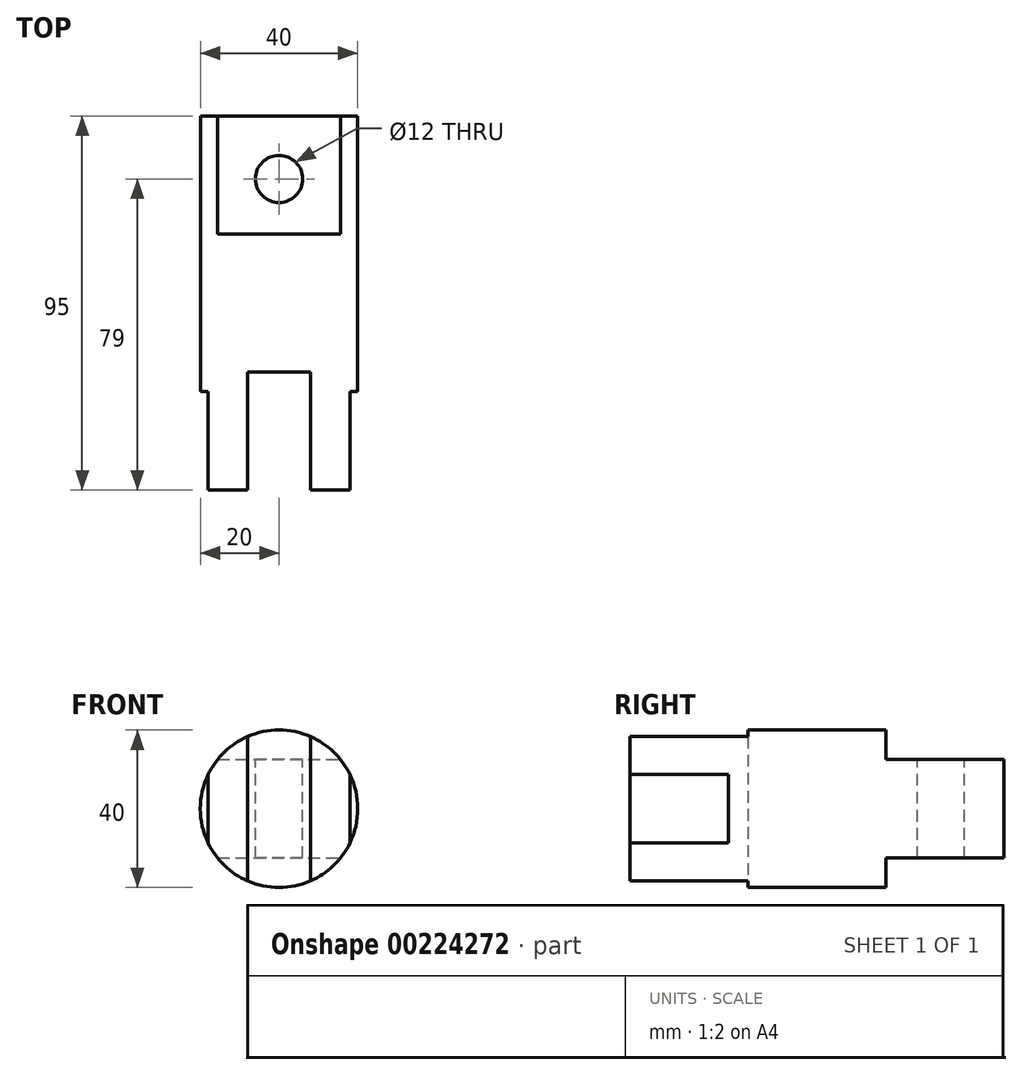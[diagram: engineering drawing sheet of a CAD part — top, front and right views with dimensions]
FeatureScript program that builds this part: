
annotation { "Feature Type Name" : "Feature", "Feature Type Description" : "" }
export const myFeature = defineFeature(function(context is Context, id is Id, definition is map)
    precondition{}
    {
        {
            var Q0;
            Q0=qCreatedBy(makeId("Front.planeOp"),FACE);
            var sketch = newSketch(context, id + "F0", { "sketchPlane" : qUnion([Q0])});
            skCircle(sketch, "E0", {"center": v(0, 0) * mm, "radius": 20 * mm});
            skSolve(sketch);
        }
        {
            var Q0;
            Q0=makeQuery(id+"F0.imprint","IMPRINT",FACE,{"disambiguationData":[TD([[makeQuery(id+"F0.imprint","IMPRINT",EDGE,{"derivedFrom":sQuery(id+"F0.wireOp",EDGE,"E0")}),1.0]])]});
            extrude(context, id + "F1", {"entities" : qUnion([Q0]), "endBound" : BoundingType.SYMMETRIC, "depth" : 95 * mm});
        }
        {
            var Q0;
            Q0=makeQuery(id+"F1.opExtrude","CAP_FACE",FACE,{"disambiguationData":[OSD([sQuery(id+"F0.wireOp",EDGE,"E0")])],"isStart":false});
            var sketch = newSketch(context, id + "F2", { "sketchPlane" : qUnion([Q0])});
            skLineSegment(sketch, "E1", {"start": v(-8, 18.33) * mm, "end": v(-8, -18.33) * mm});
            skLineSegment(sketch, "E2.MirrorCS", {"start": v(8, 18.33) * mm, "end": v(8, -18.33) * mm});
            skCircle(sketch, "E3.0", {"center": v(0, 0) * mm, "radius": 20 * mm});
            skSolve(sketch);
        }
        {
            var Q0;
            {var subQ0=sQuery(id+"F2.wireOp",EDGE,"E1");Q0=makeQuery(id+"F2.imprint","IMPRINT",FACE,{"disambiguationData":[TD([[makeQuery(id+"F2.imprint","IMPRINT",EDGE,{"derivedFrom":subQ0}),1.0]])]});}
            extrude(context, id + "F3", {"entities" : qUnion([Q0]), "operationType" : NewBodyOperationType.REMOVE, "oppositeDirection" : true, "depth" : 30 * mm});
        }
        {
            var Q0;
            {var subQ0=sQuery(id+"F2.wireOp",EDGE,"E2.MirrorCS");Q0=makeQuery(id+"F2.imprint","IMPRINT",FACE,{"disambiguationData":[TD([[makeQuery(id+"F2.imprint","IMPRINT",EDGE,{"derivedFrom":subQ0}),1.0]])]});}
            var sketch = newSketch(context, id + "F4", { "sketchPlane" : qUnion([Q0])});
            skLineSegment(sketch, "E4", {"start": v(18, 8.72) * mm, "end": v(18, -8.72) * mm});
            skCircle(sketch, "E5.0", {"center": v(0, 0) * mm, "radius": 20 * mm});
            skLineSegment(sketch, "E6.MirrorCS", {"start": v(-18, 8.72) * mm, "end": v(-18, -8.72) * mm});
            skSolve(sketch);
        }
        {
            var Q0;
            {var subQ0=sQuery(id+"F4.wireOp",EDGE,"E6.MirrorCS");Q0=makeQuery(id+"F4.imprint","IMPRINT",FACE,{"disambiguationData":[TD([[makeQuery(id+"F4.imprint","IMPRINT",EDGE,{"derivedFrom":subQ0}),-1.0]])]});}
            var Q1;
            {var subQ0=sQuery(id+"F4.wireOp",EDGE,"E4");Q1=makeQuery(id+"F4.imprint","IMPRINT",FACE,{"disambiguationData":[TD([[makeQuery(id+"F4.imprint","IMPRINT",EDGE,{"derivedFrom":subQ0}),1.0]])]});}
            extrude(context, id + "F5", {"entities" : qUnion([Q0, Q1]), "operationType" : NewBodyOperationType.REMOVE, "oppositeDirection" : true, "depth" : 25 * mm});
        }
        {
            var Q0;
            Q0=makeQuery(id+"F1.opExtrude","CAP_FACE",FACE,{"disambiguationData":[OSD([sQuery(id+"F0.wireOp",EDGE,"E0")])],"isStart":true});
            var sketch = newSketch(context, id + "F6", { "sketchPlane" : qUnion([Q0])});
            skLineSegment(sketch, "E7", {"start": v(15.61, 12.5) * mm, "end": v(-15.61, 12.5) * mm});
            skLineSegment(sketch, "E8", {"start": v(15.61, -12.5) * mm, "end": v(-15.61, -12.5) * mm});
            skCircle(sketch, "E9.0", {"center": v(0, 0) * mm, "radius": 20 * mm});
            skSolve(sketch);
        }
        {
            var Q0;
            {var subQ0=sQuery(id+"F6.wireOp",EDGE,"E7");Q0=makeQuery(id+"F6.imprint","IMPRINT",FACE,{"disambiguationData":[TD([[makeQuery(id+"F6.imprint","IMPRINT",EDGE,{"derivedFrom":subQ0}),-1.0]])]});}
            var Q1;
            {var subQ0=sQuery(id+"F6.wireOp",EDGE,"E8");Q1=makeQuery(id+"F6.imprint","IMPRINT",FACE,{"disambiguationData":[TD([[makeQuery(id+"F6.imprint","IMPRINT",EDGE,{"derivedFrom":subQ0}),1.0]])]});}
            extrude(context, id + "F7", {"entities" : qUnion([Q0, Q1]), "operationType" : NewBodyOperationType.REMOVE, "oppositeDirection" : true, "depth" : 30 * mm});
        }
        {
            var Q0;
            Q0=makeQuery(id+"F7.boolean.opBoolean","COPY",FACE,{"derivedFrom":makeQuery(id+"F7.opExtrude","SWEPT_FACE",FACE,{"disambiguationData":[OSD([sQuery(id+"F6.wireOp",EDGE,"E7")])]})});
            var sketch = newSketch(context, id + "F8", { "sketchPlane" : qUnion([Q0])});
            skCircle(sketch, "E10", {"center": v(0, 31.5) * mm, "radius": 6 * mm});
            skSolve(sketch);
        }
        {
            var Q0;
            Q0 = qSketchRegion(id + "F8", true);
            extrude(context, id + "F9", {"entities" : qUnion([Q0]), "operationType" : NewBodyOperationType.ADD, "depth" : 25 * mm});
        }
        {
            var Q0;
            Q0=makeQuery(id+"F9.opExtrude","CAP_FACE",FACE,{"disambiguationData":[OSD([sQuery(id+"F8.wireOp",EDGE,"E10")])],"isStart":false});
            extrude(context, id + "F10", {"entities" : qUnion([Q0]), "operationType" : NewBodyOperationType.REMOVE, "endBound" : BoundingType.THROUGH_ALL, "oppositeDirection" : true, "depth" : 25 * mm});
        }
    });
